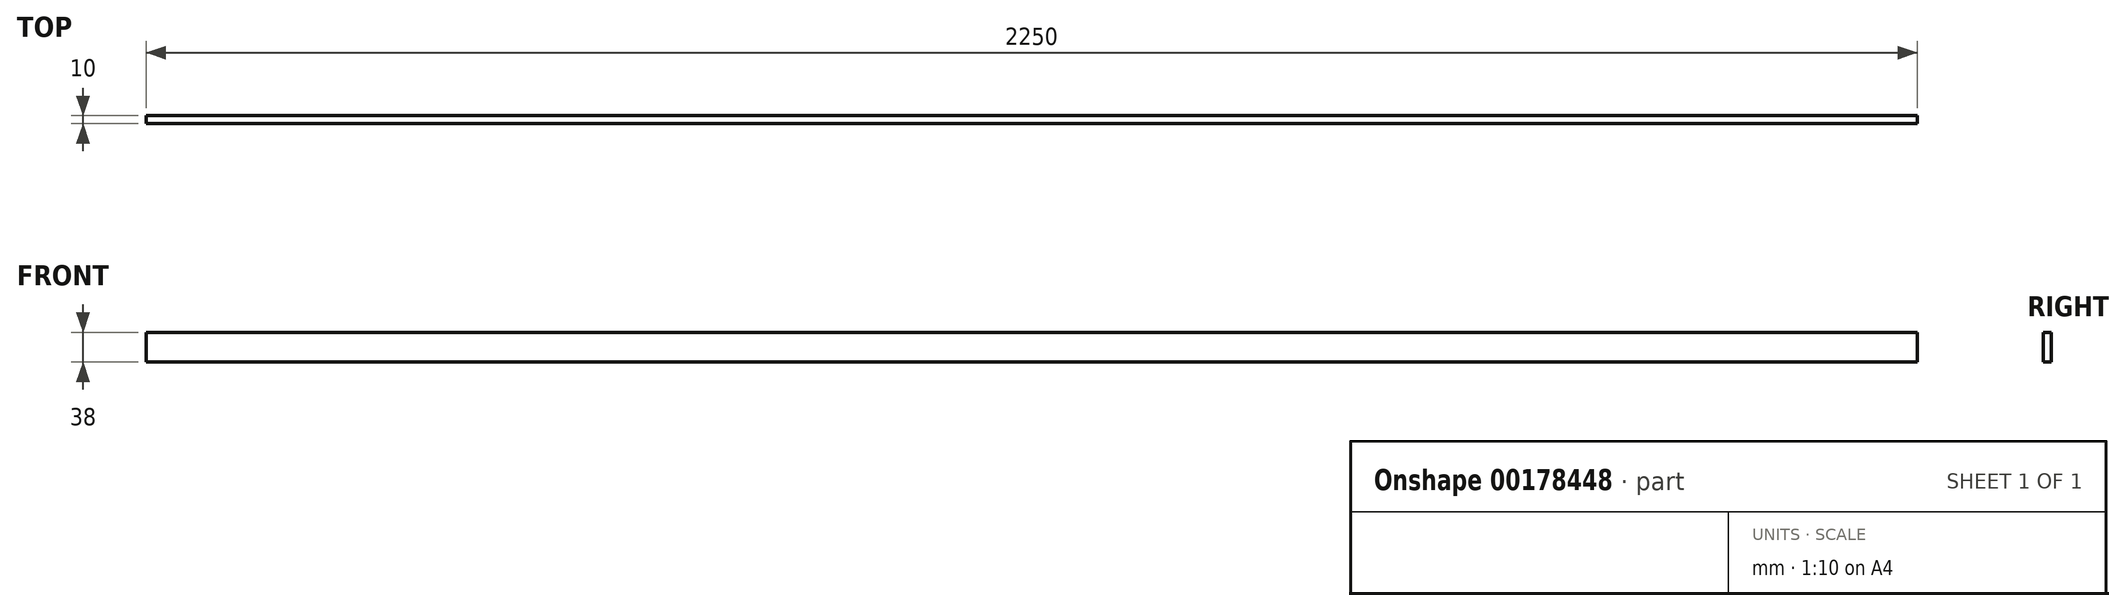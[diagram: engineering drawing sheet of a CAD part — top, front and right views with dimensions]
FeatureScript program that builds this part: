
annotation { "Feature Type Name" : "Feature", "Feature Type Description" : "" }
export const myFeature = defineFeature(function(context is Context, id is Id, definition is map)
    precondition{}
    {
        {
            var Q0;
            Q0=qCreatedBy(makeId("Front.planeOp"),FACE);
            var sketch = newSketch(context, id + "F0", { "sketchPlane" : qUnion([Q0])});
            skLineSegment(sketch, "E0.bottom", {"start": v(0, 0) * mm, "end": v(2250, 0) * mm});
            skLineSegment(sketch, "E0.top", {"start": v(0, 38) * mm, "end": v(2250, 38) * mm});
            skLineSegment(sketch, "E0.left", {"start": v(0, 0) * mm, "end": v(0, 38) * mm});
            skLineSegment(sketch, "E0.right", {"start": v(2250, 0) * mm, "end": v(2250, 38) * mm});
            skSolve(sketch);
        }
        {
            var Q0;
            Q0 = qSketchRegion(id + "F0", true);
            extrude(context, id + "F1", {"entities" : qUnion([Q0]), "depth" : 10 * mm});
        }
    });
